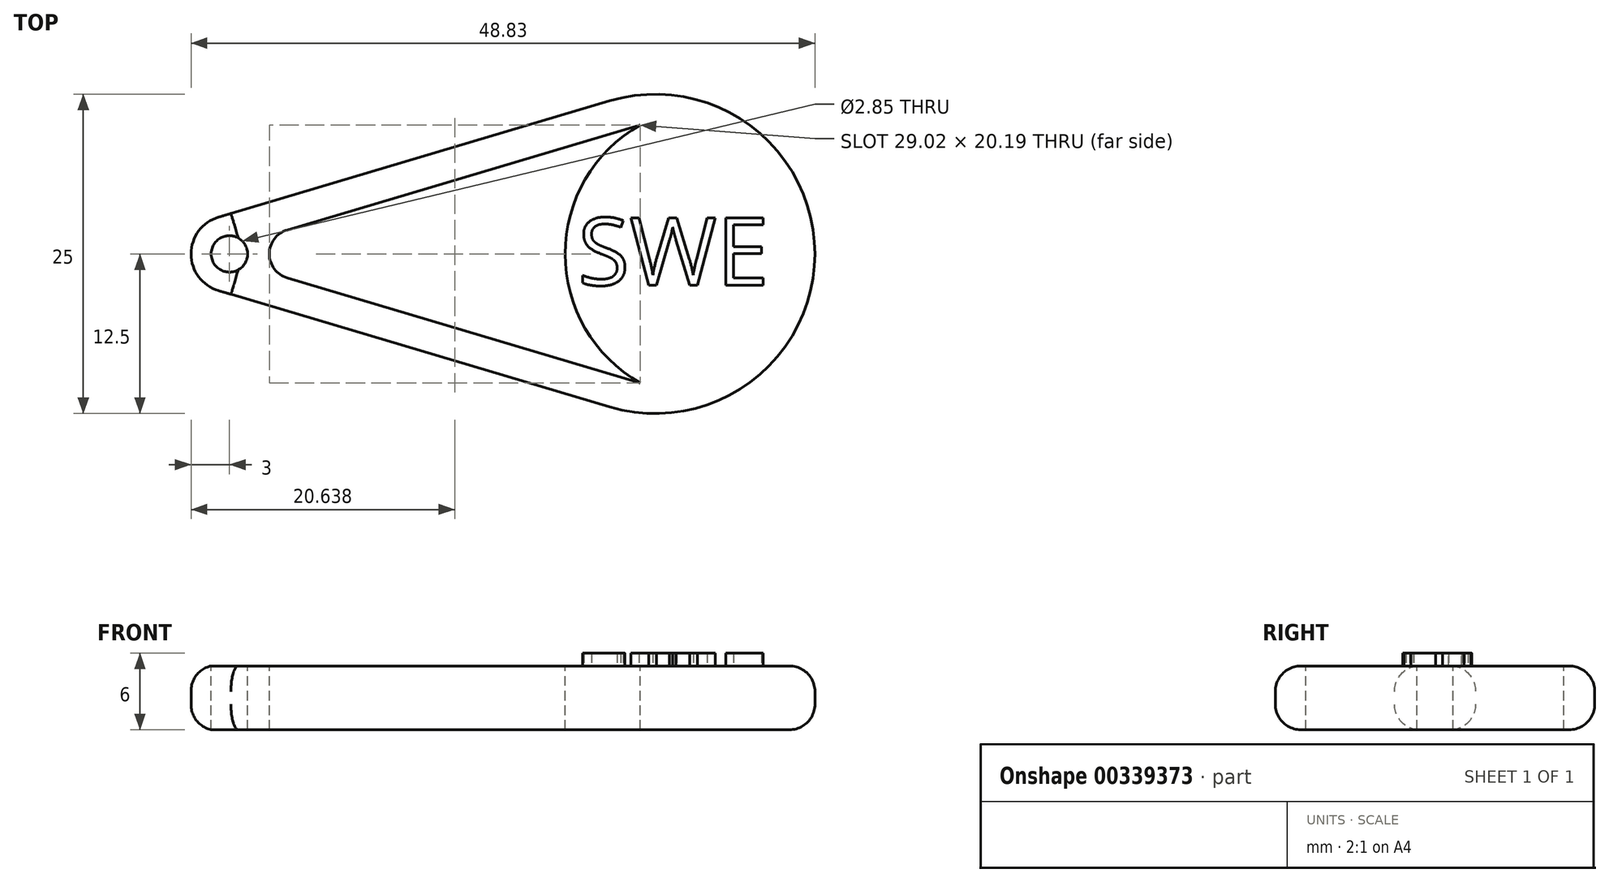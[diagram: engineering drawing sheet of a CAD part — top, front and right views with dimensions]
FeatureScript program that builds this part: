
annotation { "Feature Type Name" : "Feature", "Feature Type Description" : "" }
export const myFeature = defineFeature(function(context is Context, id is Id, definition is map)
    precondition{}
    {
        {
            var Q0;
            Q0=qCreatedBy(makeId("Top.planeOp"),FACE);
            var sketch = newSketch(context, id + "F0", { "sketchPlane" : qUnion([Q0])});
            skCircle(sketch, "E0", {"center": v(0, 0) * mm, "radius": 3 * mm});
            skCircle(sketch, "E1", {"center": v(33.33, 0) * mm, "radius": 12.5 * mm});
            skLineSegment(sketch, "E2", {"start": v(-0.86, 2.88) * mm, "end": v(29.77, 11.98) * mm});
            skLineSegment(sketch, "E3", {"start": v(-0.86, -2.88) * mm, "end": v(29.77, -11.98) * mm});
            skSolve(sketch);
        }
        {
            var Q0;
            Q0 = qSketchRegion(id + "F0", true);
            extrude(context, id + "F1", {"entities" : qUnion([Q0]), "depth" : 2.5 * mm, "hasSecondDirection" : true, "secondDirectionOppositeDirection" : true, "secondDirectionDepth" : 2.5 * mm});
        }
        {
            var Q0;
            Q0=qCreatedBy(makeId("Top.planeOp"),FACE);
            var sketch = newSketch(context, id + "F2", { "sketchPlane" : qUnion([Q0])});
            skLineSegment(sketch, "E4", {"start": v(4.53, 1.88) * mm, "end": v(32.15, 10.1) * mm});
            skLineSegment(sketch, "E5", {"start": v(4.53, -1.88) * mm, "end": v(32.15, -10.1) * mm});
            skArc(sketch, "E6", {"start": v(4.53, 1.88) * mm, "mid": v(3.13, 0) * mm, "end": v(4.53, -1.88) * mm});
            skArc(sketch, "E7", {"start": v(32.15, 10.1) * mm, "mid": v(26.28, 0) * mm, "end": v(32.15, -10.1) * mm});
            skSolve(sketch);
        }
        {
            var Q0;
            Q0=makeQuery(id+"F1.opExtrude","CAP_FACE",FACE,{"disambiguationData":[OSD([sQuery(id+"F0.wireOp",EDGE,"E0"),sQuery(id+"F0.wireOp",EDGE,"E1"),sQuery(id+"F0.wireOp",EDGE,"E2"),sQuery(id+"F0.wireOp",EDGE,"E3")])],"isStart":false});
            var sketch = newSketch(context, id + "F3", { "sketchPlane" : qUnion([Q0])});
            skCircle(sketch, "E8", {"center": v(0, 0) * mm, "radius": 1.42 * mm});
            skSolve(sketch);
        }
        {
            var Q0;
            Q0 = qSketchRegion(id + "F3", true);
            var Q1;
            Q1=makeQuery(id+"F1.opExtrude","CAP_FACE",FACE,{"disambiguationData":[OSD([sQuery(id+"F0.wireOp",EDGE,"E0"),sQuery(id+"F0.wireOp",EDGE,"E1"),sQuery(id+"F0.wireOp",EDGE,"E2"),sQuery(id+"F0.wireOp",EDGE,"E3")])],"isStart":true});
            extrude(context, id + "F4", {"entities" : qUnion([Q0]), "operationType" : NewBodyOperationType.REMOVE, "endBound" : BoundingType.UP_TO_SURFACE, "oppositeDirection" : true, "endBoundEntityFace" : qUnion([Q1]), "depth" : 25 * mm});
        }
        {
            var Q0;
            Q0 = qSketchRegion(id + "F2", true);
            var Q1;
            Q1=makeQuery(id+"F1.opExtrude","CAP_FACE",FACE,{"disambiguationData":[OSD([sQuery(id+"F0.wireOp",EDGE,"E0"),sQuery(id+"F0.wireOp",EDGE,"E1"),sQuery(id+"F0.wireOp",EDGE,"E2"),sQuery(id+"F0.wireOp",EDGE,"E3")])],"isStart":true});
            var Q2;
            Q2=makeQuery(id+"F1.opExtrude","CAP_FACE",FACE,{"disambiguationData":[OSD([sQuery(id+"F0.wireOp",EDGE,"E0"),sQuery(id+"F0.wireOp",EDGE,"E1"),sQuery(id+"F0.wireOp",EDGE,"E2"),sQuery(id+"F0.wireOp",EDGE,"E3")])],"isStart":false});
            extrude(context, id + "F5", {"entities" : qUnion([Q0]), "operationType" : NewBodyOperationType.REMOVE, "endBound" : BoundingType.UP_TO_SURFACE, "oppositeDirection" : true, "endBoundEntityFace" : qUnion([Q1]), "depth" : 25 * mm, "hasSecondDirection" : true, "secondDirectionBound" : SecondDirectionBoundingType.UP_TO_SURFACE, "secondDirectionOppositeDirection" : false, "secondDirectionBoundEntityFace" : qUnion([Q2]), "secondDirectionDepth" : 25 * mm});
        }
        {
            var Q0;
            Q0=makeQuery(id+"F1.opExtrude","CAP_FACE",FACE,{"disambiguationData":[OSD([sQuery(id+"F0.wireOp",EDGE,"E0"),sQuery(id+"F0.wireOp",EDGE,"E1"),sQuery(id+"F0.wireOp",EDGE,"E2"),sQuery(id+"F0.wireOp",EDGE,"E3")])],"isStart":false});
            var sketch = newSketch(context, id + "F6", { "sketchPlane" : qUnion([Q0])});
            skText(sketch, "E9", { "text": "SWE", "fontName": "OpenSans-Regular.ttf"});
            const initialGuessF6  = {"E9": [0.02728, -0.00244, 1, 0, 0.0053]};
            skSetInitialGuess(sketch, initialGuessF6);
            skSolve(sketch);
        }
        {
            var Q0;
            Q0 = qSketchRegion(id + "F6", true);
            extrude(context, id + "F7", {"entities" : qUnion([Q0]), "operationType" : NewBodyOperationType.ADD, "depth" : 1 * mm});
        }
        {
            var Q0;
            Q0=makeQuery(id+"F1.opExtrude","CAP_EDGE",EDGE,{"disambiguationData":[OSD([sQuery(id+"F0.wireOp",EDGE,"E3")])],"isStart":true});
            var Q1;
            Q1=makeQuery(id+"F1.opExtrude","CAP_EDGE",EDGE,{"disambiguationData":[OSD([sQuery(id+"F0.wireOp",EDGE,"E2")])],"isStart":true});
            var Q2;
            Q2=makeQuery(id+"F1.opExtrude","CAP_EDGE",EDGE,{"disambiguationData":[OSD([sQuery(id+"F0.wireOp",EDGE,"E1")])],"isStart":true});
            var Q3;
            Q3=makeQuery(id+"F1.opExtrude","CAP_EDGE",EDGE,{"disambiguationData":[OSD([sQuery(id+"F0.wireOp",EDGE,"E2")])],"isStart":false});
            var Q4;
            Q4=makeQuery(id+"F1.opExtrude","CAP_EDGE",EDGE,{"disambiguationData":[OSD([sQuery(id+"F0.wireOp",EDGE,"E1")])],"isStart":false});
            var Q5;
            Q5=makeQuery(id+"F1.opExtrude","CAP_EDGE",EDGE,{"disambiguationData":[OSD([sQuery(id+"F0.wireOp",EDGE,"E3")])],"isStart":false});
            var Q6;
            Q6=makeQuery(id+"F1.opExtrude","CAP_EDGE",EDGE,{"disambiguationData":[OSD([sQuery(id+"F0.wireOp",EDGE,"E0")])],"isStart":false});
            fillet(context, id + "F8", {"entities" : qUnion([Q0, Q1, Q2, Q3, Q4, Q5, Q6]), "radius" : 2 * mm, "tangentPropagation" : true, "allowEdgeOverflow" : false});
        }
    });
